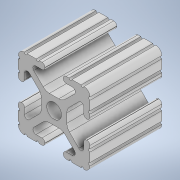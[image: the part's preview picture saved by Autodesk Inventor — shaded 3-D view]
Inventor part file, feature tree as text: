
AUTODESK INVENTOR PART (.ipt)
format: ipt  version: 2020 (Build 240168000, 168)  size: 237,056 bytes
history: native  units: in
note: dims shown in document units (in); Inventor stores cm internally (conversion verified against a paired STEP export)
features: extrude x1, sketch x1
ambient origin geometry x8: Origin, YZ Plane, XZ Plane, XY Plane, X Axis, Y Axis, Z Axis, Center Point
bodies: Solid1 (feature_tree)
feature tree (2):
  extrude  "Extrusion1"  [1 undecoded]
  sketch  "Sketch1"  dims[d0=1.0in d1=0.0in]
note: 1 required parameter value undecoded (feature->parameter linkage not recoverable at this tier; creation-order binding heuristic only, values carry confidence <= 0.55)
